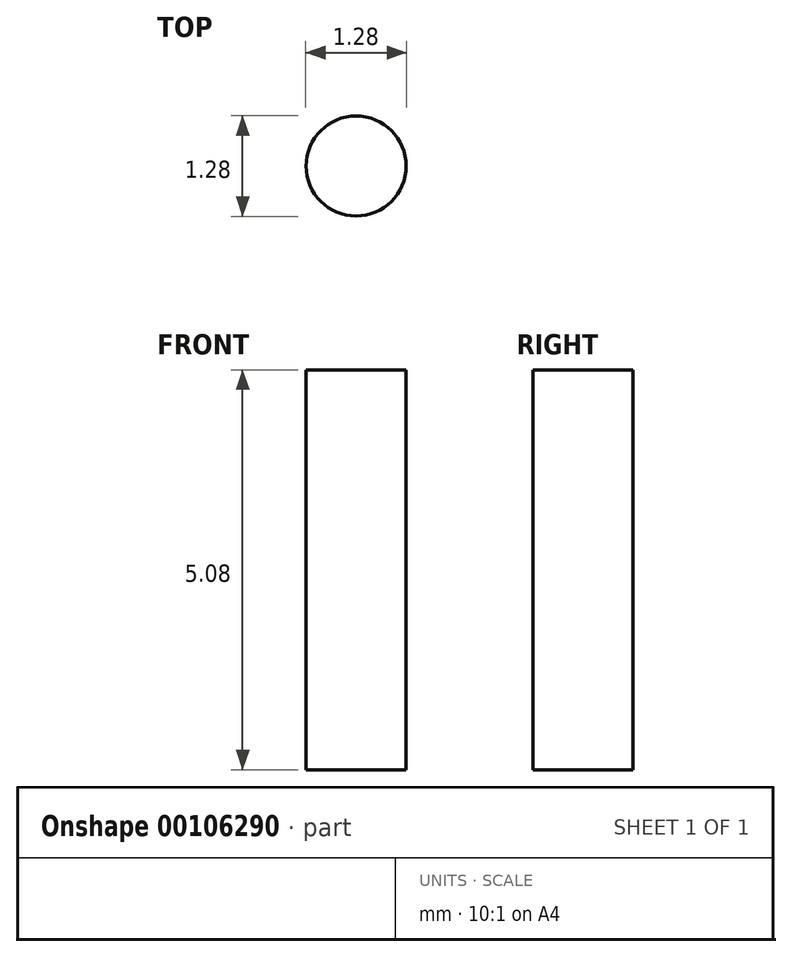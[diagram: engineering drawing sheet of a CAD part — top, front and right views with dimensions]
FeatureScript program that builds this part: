
annotation { "Feature Type Name" : "Feature", "Feature Type Description" : "" }
export const myFeature = defineFeature(function(context is Context, id is Id, definition is map)
    precondition{}
    {
        {
            var Q0;
            Q0=qCreatedBy(makeId("Top.planeOp"),FACE);
            var sketch = newSketch(context, id + "F0", { "sketchPlane" : qUnion([Q0])});
            skCircle(sketch, "E0", {"center": v(0, 0) * mm, "radius": 0.64 * mm});
            skSolve(sketch);
        }
        {
            var Q0;
            Q0 = qSketchRegion(id + "F0", true);
            extrude(context, id + "F1", {"entities" : qUnion([Q0]), "depth" : 5.08 * mm});
        }
    });
